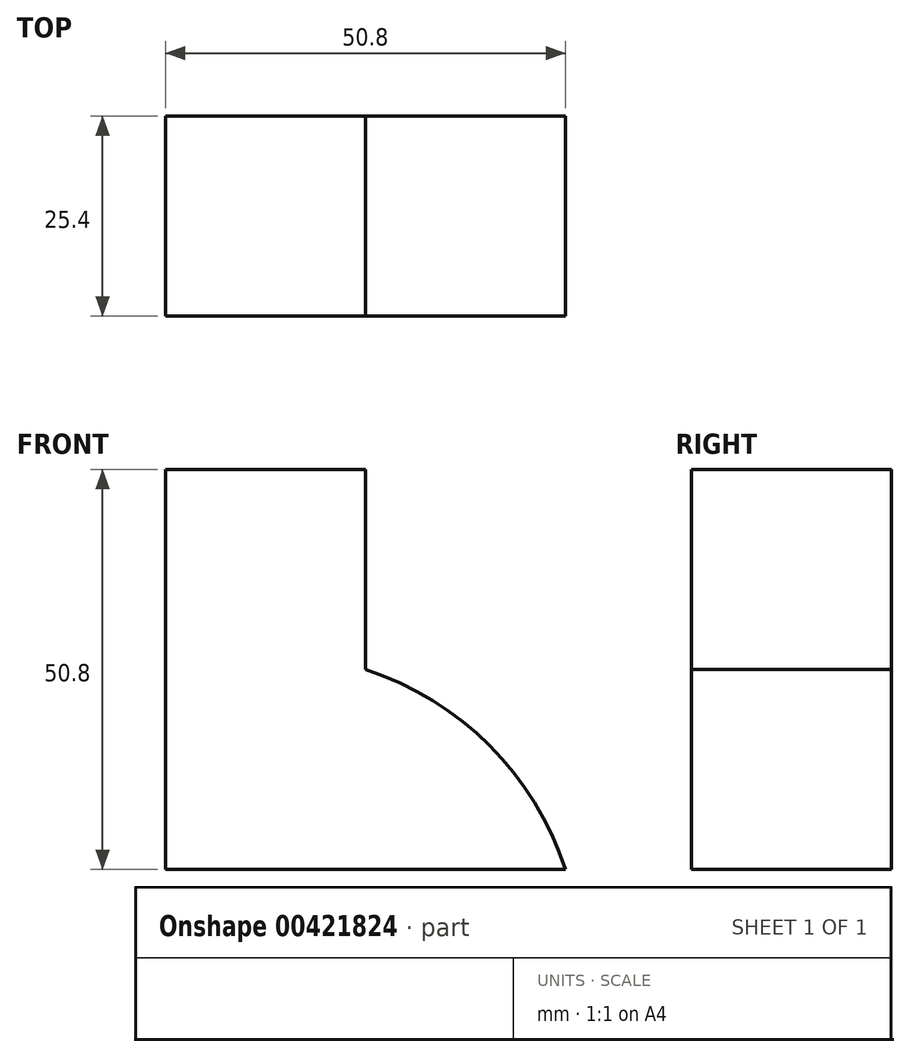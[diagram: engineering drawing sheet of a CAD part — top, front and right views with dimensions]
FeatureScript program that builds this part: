
annotation { "Feature Type Name" : "Feature", "Feature Type Description" : "" }
export const myFeature = defineFeature(function(context is Context, id is Id, definition is map)
    precondition{}
    {
        {
            var Q0;
            Q0=qCreatedBy(makeId("Front.planeOp"),FACE);
            var sketch = newSketch(context, id + "F0", { "sketchPlane" : qUnion([Q0])});
            skLineSegment(sketch, "E0", {"start": v(0, 0) * mm, "end": v(-50.8, 0) * mm});
            skLineSegment(sketch, "E1", {"start": v(-50.8, 0) * mm, "end": v(-50.8, 50.8) * mm});
            skLineSegment(sketch, "E2", {"start": v(-50.8, 50.8) * mm, "end": v(-25.4, 50.8) * mm});
            skLineSegment(sketch, "E3", {"start": v(-25.4, 50.8) * mm, "end": v(-25.4, 25.4) * mm});
            skArc(sketch, "E4", {"start": v(0, 0) * mm, "mid": v(-9.65, 15.75) * mm, "end": v(-25.4, 25.4) * mm});
            skSolve(sketch);
        }
        {
            var Q0;
            Q0 = qSketchRegion(id + "F0", true);
            extrude(context, id + "F1", {"entities" : qUnion([Q0]), "depth" : 25.4 * mm});
        }
    });
